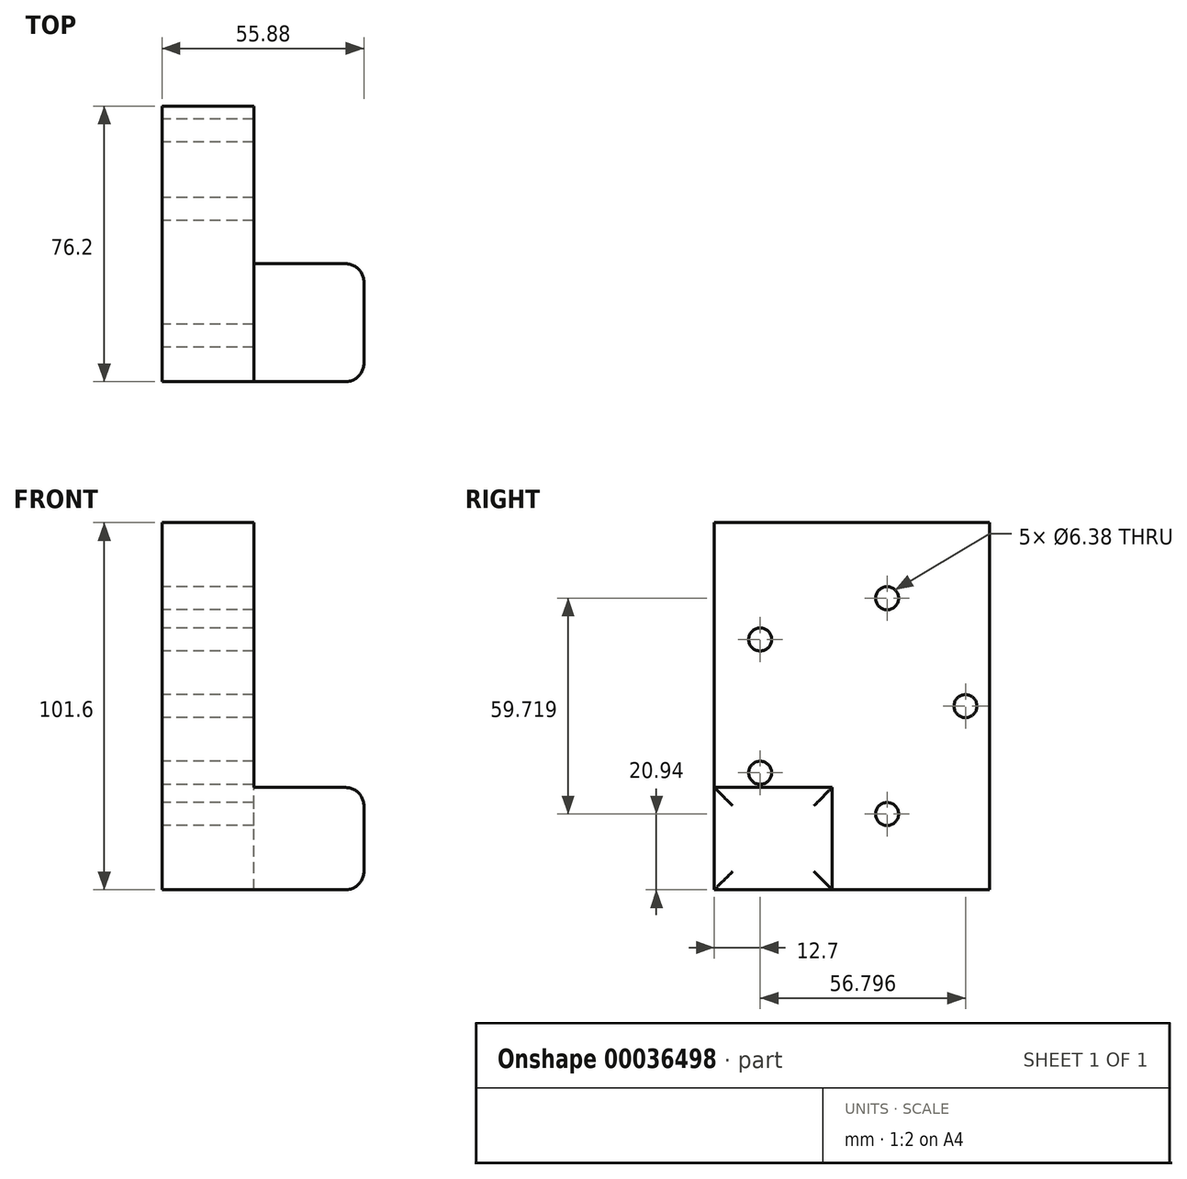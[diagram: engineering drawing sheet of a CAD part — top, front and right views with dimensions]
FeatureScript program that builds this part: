
annotation { "Feature Type Name" : "Feature", "Feature Type Description" : "" }
export const myFeature = defineFeature(function(context is Context, id is Id, definition is map)
    precondition{}
    {
        {
            var Q0;
            Q0=qCreatedBy(makeId("Right.planeOp"),FACE);
            var sketch = newSketch(context, id + "F0", { "sketchPlane" : qUnion([Q0])});
            skLineSegment(sketch, "E0.rect.bottom", {"start": v(-38.1, 50.8) * mm, "end": v(38.1, 50.8) * mm});
            skLineSegment(sketch, "E0.rect.top", {"start": v(-38.1, -50.8) * mm, "end": v(38.1, -50.8) * mm});
            skLineSegment(sketch, "E0.rect.left", {"start": v(-38.1, 50.8) * mm, "end": v(-38.1, -50.8) * mm});
            skLineSegment(sketch, "E0.rect.right", {"start": v(38.1, 50.8) * mm, "end": v(38.1, -50.8) * mm});
            skPoint(sketch, "E0.rect.middle", {"position": v(0, 0) * mm});
            skSolve(sketch);
        }
        {
            var Q0;
            Q0 = qSketchRegion(id + "F0", true);
            extrude(context, id + "F1", {"entities" : qUnion([Q0]), "depth" : 25.4 * mm});
        }
        {
            var Q0;
            Q0=makeQuery(id+"F1.opExtrude","CAP_FACE",FACE,{"disambiguationData":[OSD([sQuery(id+"F0.wireOp",EDGE,"E0.rect.bottom"),sQuery(id+"F0.wireOp",EDGE,"E0.rect.top"),sQuery(id+"F0.wireOp",EDGE,"E0.rect.left"),sQuery(id+"F0.wireOp",EDGE,"E0.rect.right")])],"isStart":true});
            var sketch = newSketch(context, id + "F2", { "sketchPlane" : qUnion([Q0])});
            skCircle(sketch, "E1.cCircle", {"center": v(0, 0) * mm, "radius": 25.4 * mm, "construction": true});
            skLineSegment(sketch, "E1.0", {"start": v(-31.4, 0) * mm, "end": v(-9.7, 29.86) * mm});
            skLineSegment(sketch, "E1.1", {"start": v(-9.7, 29.86) * mm, "end": v(25.4, 18.45) * mm});
            skLineSegment(sketch, "E1.2", {"start": v(25.4, 18.45) * mm, "end": v(25.4, -18.45) * mm});
            skLineSegment(sketch, "E1.3", {"start": v(25.4, -18.45) * mm, "end": v(-9.7, -29.86) * mm});
            skLineSegment(sketch, "E1.4", {"start": v(-9.7, -29.86) * mm, "end": v(-31.4, 0) * mm});
            skPoint(sketch, "E1.0.midPoint", {"position": v(-20.55, 14.93) * mm});
            skPoint(sketch, "E2", {"position": v(-9.7, -29.86) * mm});
            skPoint(sketch, "E3", {"position": v(-31.4, 0) * mm});
            skPoint(sketch, "E4", {"position": v(-9.7, 29.86) * mm});
            skPoint(sketch, "E5", {"position": v(25.4, 18.45) * mm});
            skPoint(sketch, "E6", {"position": v(25.4, -18.45) * mm});
            skSolve(sketch);
        }
        {
            var Q0;
            Q0=sQuery(id+"F2.wireOp",VERTEX,"E3");
            var Q1;
            Q1=sQuery(id+"F2.wireOp",VERTEX,"E4");
            var Q2;
            Q2=sQuery(id+"F2.wireOp",VERTEX,"E5");
            var Q3;
            Q3=sQuery(id+"F2.wireOp",VERTEX,"E6");
            var Q4;
            Q4=sQuery(id+"F2.wireOp",VERTEX,"E2");
            var Q5;
            Q5=makeQuery(id+"F1.opExtrude","SWEPT_BODY",BODY,{"disambiguationData":[OSD([sQuery(id+"F0.wireOp",EDGE,"E0.rect.bottom"),sQuery(id+"F0.wireOp",EDGE,"E0.rect.top"),sQuery(id+"F0.wireOp",EDGE,"E0.rect.left"),sQuery(id+"F0.wireOp",EDGE,"E0.rect.right")])]});
            hole(context, id + "F3", {"style" : HoleStyle.SIMPLE, "holeDiameter" : 6.38 * mm, "endStyle" : HoleEndStyle.THROUGH, "locations" : qUnion([Q0, Q1, Q2, Q3, Q4]), "scope" : qUnion([Q5])});
        }
        {
            var Q0;
            Q0=makeQuery(id+"F1.opExtrude","CAP_FACE",FACE,{"disambiguationData":[OSD([sQuery(id+"F0.wireOp",EDGE,"E0.rect.bottom"),sQuery(id+"F0.wireOp",EDGE,"E0.rect.top"),sQuery(id+"F0.wireOp",EDGE,"E0.rect.left"),sQuery(id+"F0.wireOp",EDGE,"E0.rect.right")])],"isStart":false});
            var sketch = newSketch(context, id + "F4", { "sketchPlane" : qUnion([Q0])});
            skLineSegment(sketch, "E7.bottom", {"start": v(-38.1, -50.8) * mm, "end": v(-5.48, -50.8) * mm});
            skLineSegment(sketch, "E7.top", {"start": v(-38.1, -22.52) * mm, "end": v(-5.48, -22.52) * mm});
            skLineSegment(sketch, "E7.left", {"start": v(-38.1, -50.8) * mm, "end": v(-38.1, -22.52) * mm});
            skLineSegment(sketch, "E7.right", {"start": v(-5.48, -50.8) * mm, "end": v(-5.48, -22.52) * mm});
            skSolve(sketch);
        }
        {
            var Q0;
            Q0=makeQuery(id+"F4.imprint","IMPRINT",FACE,{"disambiguationData":[TD([[makeQuery(id+"F4.imprint","IMPRINT",EDGE,{"derivedFrom":sQuery(id+"F4.wireOp",EDGE,"E7.bottom")}),1.0]])]});
            extrude(context, id + "F5", {"entities" : qUnion([Q0]), "operationType" : NewBodyOperationType.ADD, "depth" : 30.48 * mm, "offsetDistance" : 25.4 * mm});
        }
        {
            var Q0;
            Q0=makeQuery(id+"F5.opExtrude","CAP_EDGE",EDGE,{"disambiguationData":[OSD([sQuery(id+"F4.wireOp",EDGE,"E7.right")])],"isStart":false});
            var Q1;
            Q1=makeQuery(id+"F5.opExtrude","CAP_EDGE",EDGE,{"disambiguationData":[OSD([sQuery(id+"F4.wireOp",EDGE,"E7.bottom")])],"isStart":false});
            var Q2;
            Q2=makeQuery(id+"F5.opExtrude","CAP_EDGE",EDGE,{"disambiguationData":[OSD([sQuery(id+"F4.wireOp",EDGE,"E7.left")])],"isStart":false});
            var Q3;
            Q3=makeQuery(id+"F5.opExtrude","CAP_EDGE",EDGE,{"disambiguationData":[OSD([sQuery(id+"F4.wireOp",EDGE,"E7.top")])],"isStart":false});
            var Q4;
            Q4=makeQuery(id+"F5.opExtrude","CAP_EDGE",EDGE,{"disambiguationData":[OSD([sQuery(id+"F4.wireOp",EDGE,"E7.right")])],"isStart":true});
            var Q5;
            Q5=makeQuery(id+"F5.opExtrude","CAP_EDGE",EDGE,{"disambiguationData":[OSD([sQuery(id+"F4.wireOp",EDGE,"E7.top")])],"isStart":true});
            fillet(context, id + "F6", {"entities" : qUnion([Q0, Q1, Q2, Q3, Q4, Q5]), "radius" : 5.08 * mm, "tangentPropagation" : true, "allowEdgeOverflow" : false});
        }
    });
